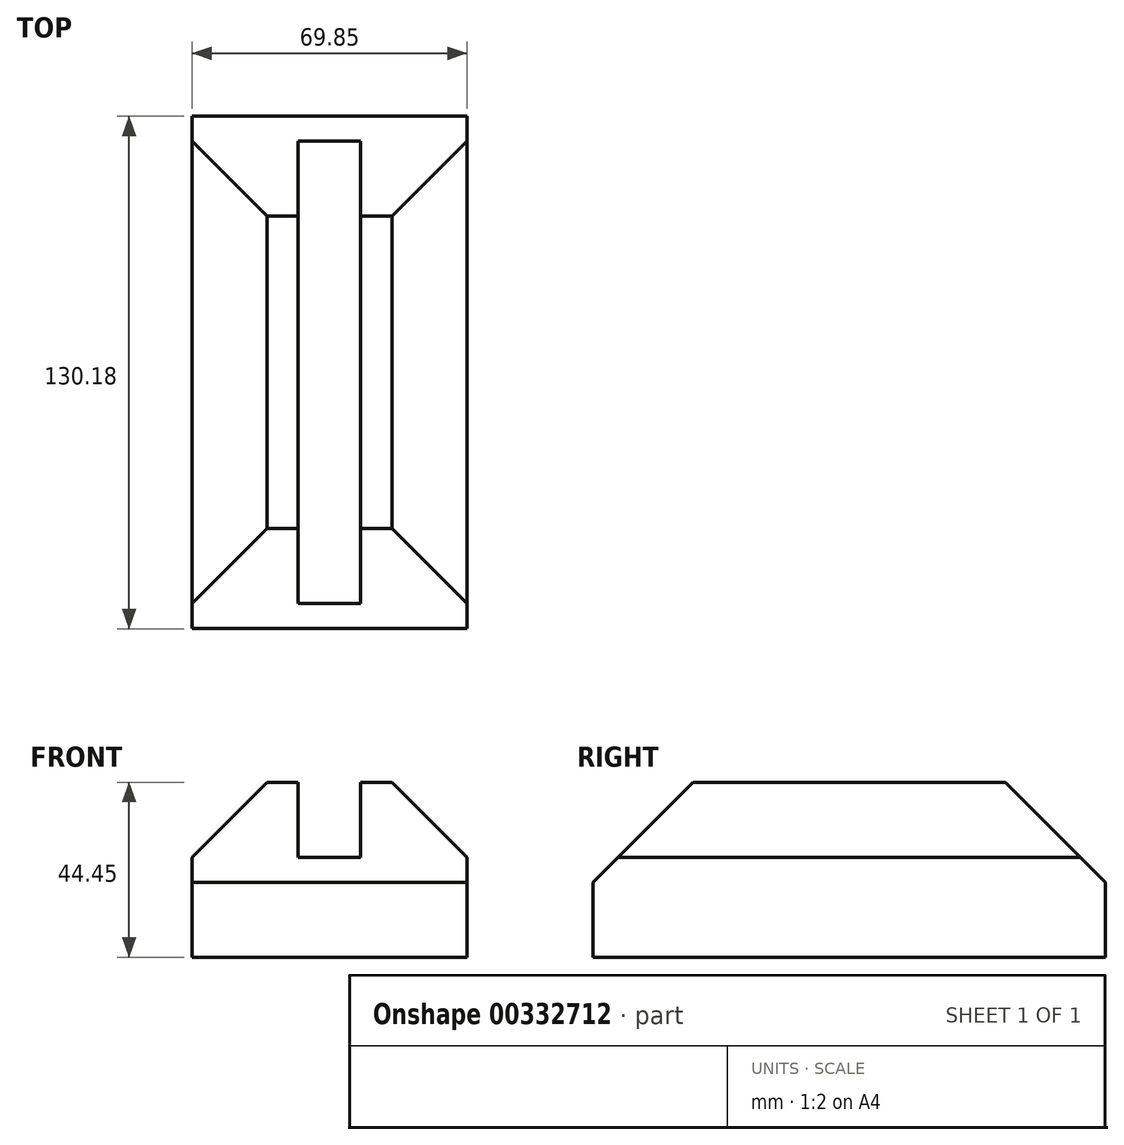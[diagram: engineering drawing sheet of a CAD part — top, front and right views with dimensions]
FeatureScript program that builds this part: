
annotation { "Feature Type Name" : "Feature", "Feature Type Description" : "" }
export const myFeature = defineFeature(function(context is Context, id is Id, definition is map)
    precondition{}
    {
        {
            var Q0;
            Q0=qCreatedBy(makeId("Front.planeOp"),FACE);
            var sketch = newSketch(context, id + "F0", { "sketchPlane" : qUnion([Q0])});
            skLineSegment(sketch, "E0", {"start": v(0, 0) * mm, "end": v(0, 25.4) * mm});
            skLineSegment(sketch, "E1", {"start": v(0, 25.4) * mm, "end": v(19.05, 44.45) * mm});
            skLineSegment(sketch, "E2", {"start": v(19.05, 44.45) * mm, "end": v(26.99, 44.45) * mm});
            skLineSegment(sketch, "E3", {"start": v(26.99, 44.45) * mm, "end": v(26.99, 25.4) * mm});
            skLineSegment(sketch, "E4", {"start": v(26.99, 25.4) * mm, "end": v(42.86, 25.4) * mm});
            skLineSegment(sketch, "E5", {"start": v(42.86, 25.4) * mm, "end": v(42.86, 44.45) * mm});
            skLineSegment(sketch, "E6", {"start": v(42.86, 44.45) * mm, "end": v(50.8, 44.45) * mm});
            skLineSegment(sketch, "E7", {"start": v(50.8, 44.45) * mm, "end": v(69.85, 25.4) * mm});
            skLineSegment(sketch, "E8", {"start": v(69.85, 25.4) * mm, "end": v(69.85, 0) * mm});
            skLineSegment(sketch, "E9", {"start": v(69.85, 0) * mm, "end": v(0, 0) * mm});
            skSolve(sketch);
        }
        {
            var Q0;
            Q0 = qSketchRegion(id + "F0", true);
            extrude(context, id + "F1", {"entities" : qUnion([Q0]), "depth" : 130.17 * mm});
        }
        {
            var Q0;
            Q0=makeQuery(id+"F1.opExtrude","CAP_EDGE",EDGE,{"disambiguationData":[OSD([sQuery(id+"F0.wireOp",EDGE,"E6")])],"isStart":false});
            var Q1;
            Q1=makeQuery(id+"F1.opExtrude","CAP_EDGE",EDGE,{"disambiguationData":[OSD([sQuery(id+"F0.wireOp",EDGE,"E2")])],"isStart":false});
            var Q2;
            Q2=makeQuery(id+"F1.opExtrude","CAP_EDGE",EDGE,{"disambiguationData":[OSD([sQuery(id+"F0.wireOp",EDGE,"E2")])],"isStart":true});
            var Q3;
            Q3=makeQuery(id+"F1.opExtrude","CAP_EDGE",EDGE,{"disambiguationData":[OSD([sQuery(id+"F0.wireOp",EDGE,"E6")])],"isStart":true});
            chamfer(context, id + "F2", {"entities" : qUnion([Q0, Q1, Q2, Q3]), "width" : 25.4 * mm, "tangentPropagation" : true});
        }
    });
